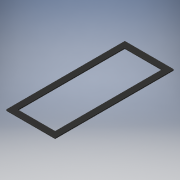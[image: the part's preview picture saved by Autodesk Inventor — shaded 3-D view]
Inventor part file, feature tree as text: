
AUTODESK INVENTOR PART (.ipt)
format: ipt  version: 2019 (Build 230136000, 136)  size: 118,784 bytes
history: native  units: mm
features: extrude x1, sketch x1
ambient origin geometry x8: Origin, YZ Plane, XZ Plane, XY Plane, X Axis, Y Axis, Z Axis, Center Point
bodies: Solid1 (feature_tree)
feature tree (2):
  extrude  "Extrusion1"  Depth=8.0mm
  sketch  "Sketch1"  dims[d0=8.0mm d1=8.0mm d2=70.0mm d3=170.0mm d4=1.5875mm d5=0.0mm]
